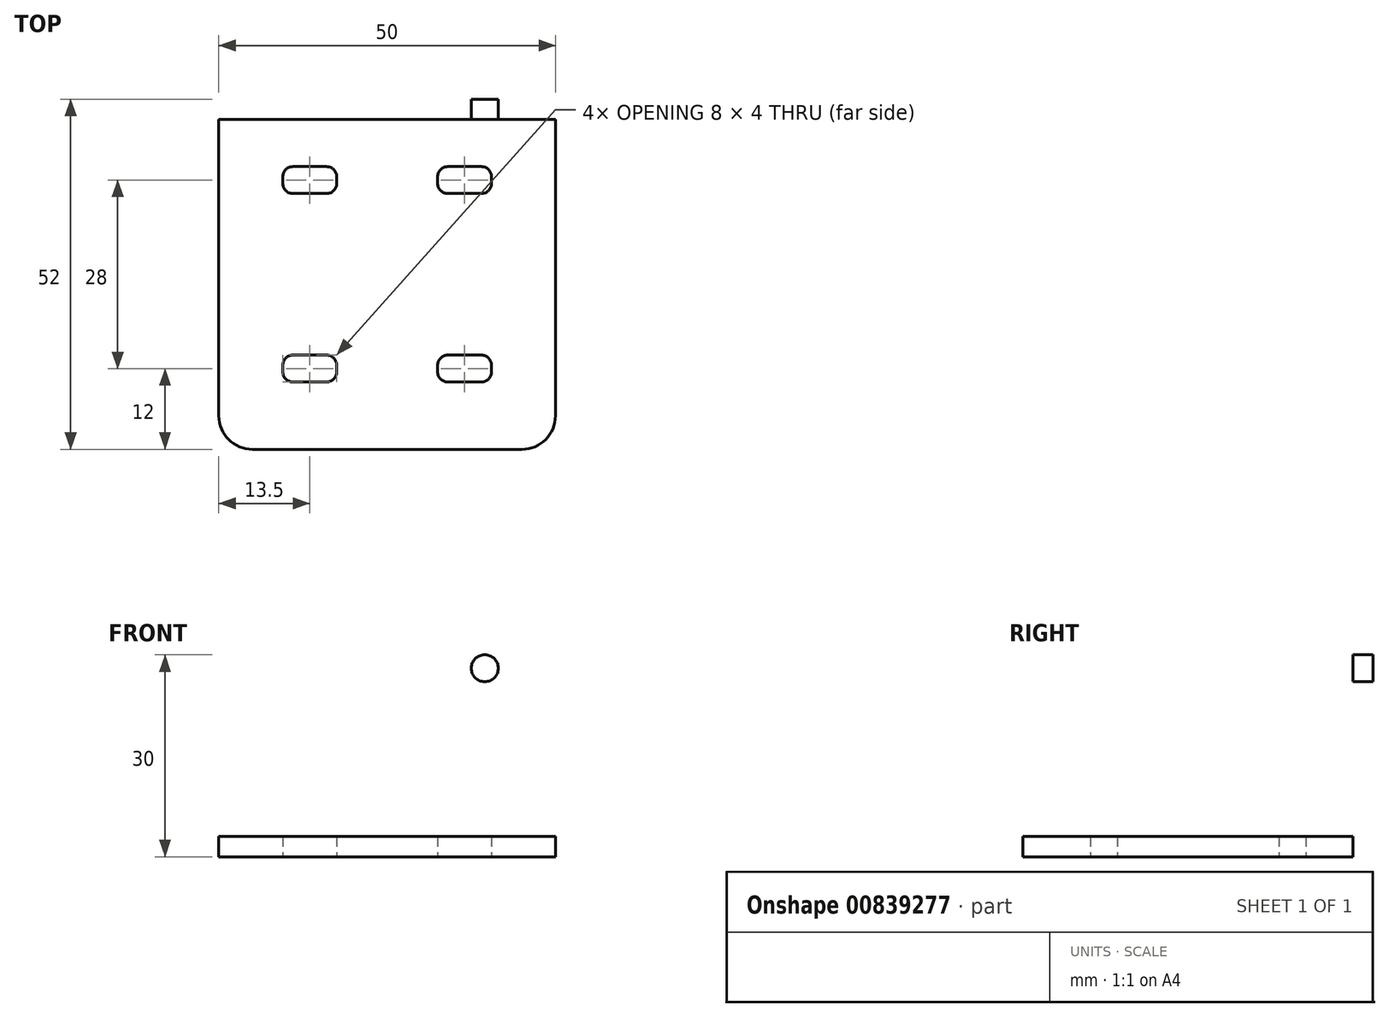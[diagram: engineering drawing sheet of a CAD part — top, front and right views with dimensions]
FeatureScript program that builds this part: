
annotation { "Feature Type Name" : "Feature", "Feature Type Description" : "" }
export const myFeature = defineFeature(function(context is Context, id is Id, definition is map)
    precondition{}
    {
        {
            var Q0;
            Q0=qCreatedBy(makeId("Top.planeOp"),FACE);
            var sketch = newSketch(context, id + "F0", { "sketchPlane" : qUnion([Q0])});
            skLineSegment(sketch, "E0", {"start": v(0, 0) * mm, "end": v(25, 0) * mm});
            skLineSegment(sketch, "E1", {"start": v(25, 0) * mm, "end": v(25, -52) * mm});
            skLineSegment(sketch, "E2", {"start": v(25, -52) * mm, "end": v(-25, -52) * mm});
            skLineSegment(sketch, "E3", {"start": v(-25, -52) * mm, "end": v(-25, 0) * mm});
            skLineSegment(sketch, "E4", {"start": v(-25, 0) * mm, "end": v(0, 0) * mm});
            skLineSegment(sketch, "E5.bottom", {"start": v(-9, -42) * mm, "end": v(-14, -42) * mm});
            skLineSegment(sketch, "E5.top", {"start": v(-9, -38) * mm, "end": v(-14, -38) * mm});
            skLineSegment(sketch, "E5.left", {"start": v(-7.5, -40.5) * mm, "end": v(-7.5, -39.5) * mm});
            skLineSegment(sketch, "E5.right", {"start": v(-15.5, -40.5) * mm, "end": v(-15.5, -39.5) * mm});
            skPoint(sketch, "E5.middle", {"position": v(-11.5, -40) * mm});
            skLineSegment(sketch, "E6.MirrorCS", {"start": v(15.5, -40.5) * mm, "end": v(15.5, -39.5) * mm});
            skPoint(sketch, "E7.MirrorP", {"position": v(11.5, -40) * mm});
            skLineSegment(sketch, "E8.MirrorCS", {"start": v(9, -38) * mm, "end": v(14, -38) * mm});
            skLineSegment(sketch, "E9.MirrorCS", {"start": v(7.5, -40.5) * mm, "end": v(7.5, -39.5) * mm});
            skLineSegment(sketch, "E10.MirrorCS", {"start": v(9, -42) * mm, "end": v(14, -42) * mm});
            skLineSegment(sketch, "E11", {"start": v(25, -26) * mm, "end": v(-25, -26) * mm});
            skLineSegment(sketch, "E12.MirrorCS", {"start": v(-9, -14) * mm, "end": v(-14, -14) * mm});
            skLineSegment(sketch, "E13.MirrorCS", {"start": v(-15.5, -11.5) * mm, "end": v(-15.5, -12.5) * mm});
            skLineSegment(sketch, "E14.MirrorCS", {"start": v(9, -14) * mm, "end": v(14, -14) * mm});
            skLineSegment(sketch, "E15.MirrorCS", {"start": v(9, -10) * mm, "end": v(14, -10) * mm});
            skLineSegment(sketch, "E16.MirrorCS", {"start": v(-9, -10) * mm, "end": v(-14, -10) * mm});
            skLineSegment(sketch, "E17.MirrorCS", {"start": v(-7.5, -11.5) * mm, "end": v(-7.5, -12.5) * mm});
            skPoint(sketch, "E18.MirrorP", {"position": v(-11.5, -12) * mm});
            skLineSegment(sketch, "E19.MirrorCS", {"start": v(7.5, -11.5) * mm, "end": v(7.5, -12.5) * mm});
            skPoint(sketch, "E20.MirrorP", {"position": v(11.5, -12) * mm});
            skLineSegment(sketch, "E21.MirrorCS", {"start": v(15.5, -11.5) * mm, "end": v(15.5, -12.5) * mm});
            skPoint(sketch, "E22.visualSharp", {"position": v(-15.5, -38) * mm});
            skArc(sketch, "E22.filletArc", {"start": v(-14, -38) * mm, "mid": v(-15.06, -38.44) * mm, "end": v(-15.5, -39.5) * mm});
            skPoint(sketch, "E23.visualSharp", {"position": v(-15.5, -42) * mm});
            skArc(sketch, "E23.filletArc", {"start": v(-15.5, -40.5) * mm, "mid": v(-15.06, -41.56) * mm, "end": v(-14, -42) * mm});
            skPoint(sketch, "E24.visualSharp", {"position": v(-7.5, -38) * mm});
            skArc(sketch, "E24.filletArc", {"start": v(-7.5, -39.5) * mm, "mid": v(-7.94, -38.44) * mm, "end": v(-9, -38) * mm});
            skPoint(sketch, "E25.visualSharp", {"position": v(-7.5, -42) * mm});
            skArc(sketch, "E25.filletArc", {"start": v(-9, -42) * mm, "mid": v(-7.94, -41.56) * mm, "end": v(-7.5, -40.5) * mm});
            skPoint(sketch, "E26.visualSharp", {"position": v(7.5, -38) * mm});
            skArc(sketch, "E26.filletArc", {"start": v(9, -38) * mm, "mid": v(7.94, -38.44) * mm, "end": v(7.5, -39.5) * mm});
            skPoint(sketch, "E27.visualSharp", {"position": v(7.5, -42) * mm});
            skArc(sketch, "E27.filletArc", {"start": v(7.5, -40.5) * mm, "mid": v(7.94, -41.56) * mm, "end": v(9, -42) * mm});
            skPoint(sketch, "E28.visualSharp", {"position": v(15.5, -42) * mm});
            skArc(sketch, "E28.filletArc", {"start": v(14, -42) * mm, "mid": v(15.06, -41.56) * mm, "end": v(15.5, -40.5) * mm});
            skPoint(sketch, "E29.visualSharp", {"position": v(15.5, -38) * mm});
            skArc(sketch, "E29.filletArc", {"start": v(15.5, -39.5) * mm, "mid": v(15.06, -38.44) * mm, "end": v(14, -38) * mm});
            skPoint(sketch, "E30.visualSharp", {"position": v(7.5, -10) * mm});
            skArc(sketch, "E30.filletArc", {"start": v(9, -10) * mm, "mid": v(7.94, -10.44) * mm, "end": v(7.5, -11.5) * mm});
            skPoint(sketch, "E31.visualSharp", {"position": v(7.5, -14) * mm});
            skArc(sketch, "E31.filletArc", {"start": v(7.5, -12.5) * mm, "mid": v(7.94, -13.56) * mm, "end": v(9, -14) * mm});
            skPoint(sketch, "E32.visualSharp", {"position": v(15.5, -14) * mm});
            skArc(sketch, "E32.filletArc", {"start": v(14, -14) * mm, "mid": v(15.06, -13.56) * mm, "end": v(15.5, -12.5) * mm});
            skPoint(sketch, "E33.visualSharp", {"position": v(15.5, -10) * mm});
            skArc(sketch, "E33.filletArc", {"start": v(15.5, -11.5) * mm, "mid": v(15.06, -10.44) * mm, "end": v(14, -10) * mm});
            skPoint(sketch, "E34.visualSharp", {"position": v(-7.5, -10) * mm});
            skArc(sketch, "E34.filletArc", {"start": v(-7.5, -11.5) * mm, "mid": v(-7.94, -10.44) * mm, "end": v(-9, -10) * mm});
            skPoint(sketch, "E35.visualSharp", {"position": v(-7.5, -14) * mm});
            skArc(sketch, "E35.filletArc", {"start": v(-9, -14) * mm, "mid": v(-7.94, -13.56) * mm, "end": v(-7.5, -12.5) * mm});
            skPoint(sketch, "E36.visualSharp", {"position": v(-15.5, -14) * mm});
            skArc(sketch, "E36.filletArc", {"start": v(-15.5, -12.5) * mm, "mid": v(-15.06, -13.56) * mm, "end": v(-14, -14) * mm});
            skPoint(sketch, "E37.visualSharp", {"position": v(-15.5, -10) * mm});
            skArc(sketch, "E37.filletArc", {"start": v(-14, -10) * mm, "mid": v(-15.06, -10.44) * mm, "end": v(-15.5, -11.5) * mm});
            skSolve(sketch);
        }
        {
            var Q0;
            {var subQ1=sQuery(id+"F0.wireOp",EDGE,"E0");Q0=makeQuery(id+"F0.imprint","IMPRINT",FACE,{"disambiguationData":[TD([[makeQuery(id+"F0.imprint","IMPRINT",EDGE,{"derivedFrom":subQ1}),-1.0]])]});}
            var Q1;
            {var subQ0=sQuery(id+"F0.wireOp",EDGE,"E2");Q1=makeQuery(id+"F0.imprint","IMPRINT",FACE,{"disambiguationData":[TD([[makeQuery(id+"F0.imprint","IMPRINT",EDGE,{"derivedFrom":subQ0}),-1.0]])]});}
            extrude(context, id + "F1", {"entities" : qUnion([Q0, Q1]), "depth" : 3 * mm, "offsetDistance" : 25 * mm});
        }
        {
            var Q0;
            Q0=makeQuery(id+"F1.opExtrude","CAP_FACE",FACE,{"disambiguationData":[OSD([sQuery(id+"F0.wireOp",EDGE,"E0"),sQuery(id+"F0.wireOp",EDGE,"E1"),sQuery(id+"F0.wireOp",EDGE,"E2"),sQuery(id+"F0.wireOp",EDGE,"E3"),sQuery(id+"F0.wireOp",EDGE,"E4"),sQuery(id+"F0.wireOp",EDGE,"E5.bottom"),sQuery(id+"F0.wireOp",EDGE,"E5.top"),sQuery(id+"F0.wireOp",EDGE,"E5.left"),sQuery(id+"F0.wireOp",EDGE,"E5.right"),sQuery(id+"F0.wireOp",EDGE,"E6.MirrorCS"),sQuery(id+"F0.wireOp",EDGE,"E8.MirrorCS"),sQuery(id+"F0.wireOp",EDGE,"E9.MirrorCS"),sQuery(id+"F0.wireOp",EDGE,"E10.MirrorCS"),sQuery(id+"F0.wireOp",EDGE,"E12.MirrorCS"),sQuery(id+"F0.wireOp",EDGE,"E13.MirrorCS"),sQuery(id+"F0.wireOp",EDGE,"E14.MirrorCS"),sQuery(id+"F0.wireOp",EDGE,"E15.MirrorCS"),sQuery(id+"F0.wireOp",EDGE,"E16.MirrorCS"),sQuery(id+"F0.wireOp",EDGE,"E17.MirrorCS"),sQuery(id+"F0.wireOp",EDGE,"E19.MirrorCS"),sQuery(id+"F0.wireOp",EDGE,"E21.MirrorCS"),sQuery(id+"F0.wireOp",EDGE,"E22.filletArc"),sQuery(id+"F0.wireOp",EDGE,"E23.filletArc"),sQuery(id+"F0.wireOp",EDGE,"E24.filletArc"),sQuery(id+"F0.wireOp",EDGE,"E25.filletArc"),sQuery(id+"F0.wireOp",EDGE,"E26.filletArc"),sQuery(id+"F0.wireOp",EDGE,"E27.filletArc"),sQuery(id+"F0.wireOp",EDGE,"E28.filletArc"),sQuery(id+"F0.wireOp",EDGE,"E29.filletArc"),sQuery(id+"F0.wireOp",EDGE,"E30.filletArc"),sQuery(id+"F0.wireOp",EDGE,"E31.filletArc"),sQuery(id+"F0.wireOp",EDGE,"E32.filletArc"),sQuery(id+"F0.wireOp",EDGE,"E33.filletArc"),sQuery(id+"F0.wireOp",EDGE,"E34.filletArc"),sQuery(id+"F0.wireOp",EDGE,"E35.filletArc"),sQuery(id+"F0.wireOp",EDGE,"E36.filletArc"),sQuery(id+"F0.wireOp",EDGE,"E37.filletArc")])],"isStart":false});
            var sketch = newSketch(context, id + "F2", { "sketchPlane" : qUnion([Q0])});
            skLineSegment(sketch, "E38.bottom", {"start": v(-25, 0) * mm, "end": v(25, 0) * mm});
            skLineSegment(sketch, "E38.top", {"start": v(-25, -3) * mm, "end": v(25, -3) * mm});
            skLineSegment(sketch, "E38.left", {"start": v(-25, 0) * mm, "end": v(-25, -3) * mm});
            skLineSegment(sketch, "E38.right", {"start": v(25, 0) * mm, "end": v(25, -3) * mm});
            skSolve(sketch);
        }
        {
            var Q0;
            Q0=makeQuery(id+"F2.imprint","IMPRINT",FACE,{"disambiguationData":[TD([[makeQuery(id+"F2.imprint","IMPRINT",EDGE,{"derivedFrom":sQuery(id+"F2.wireOp",EDGE,"E38.bottom")}),-1.0]])]});
            extrude(context, id + "F3", {"entities" : qUnion([Q0]), "operationType" : NewBodyOperationType.ADD, "depth" : 49 * mm, "offsetDistance" : 25 * mm});
        }
        {
            var Q0;
            Q0=makeQuery(id+"F3.boolean.opBoolean","MERGE",FACE,{"derivedFrom":[makeQuery(id+"F1.opExtrude","SWEPT_FACE",FACE,{"disambiguationData":[OSD([sQuery(id+"F0.wireOp",EDGE,"E0"),sQuery(id+"F0.wireOp",EDGE,"E4")])]}),makeQuery(id+"F3.opExtrude","SWEPT_FACE",FACE,{"disambiguationData":[OSD([sQuery(id+"F2.wireOp",EDGE,"E38.bottom")])]})]});
            var sketch = newSketch(context, id + "F4", { "sketchPlane" : qUnion([Q0])});
            skCircle(sketch, "E39", {"center": v(0, 28) * mm, "radius": 8.8 * mm});
            skCircle(sketch, "E40", {"center": v(14.5, 28) * mm, "radius": 2 * mm});
            skCircle(sketch, "E41.MirrorC", {"center": v(-14.5, 28) * mm, "radius": 2 * mm});
            skSolve(sketch);
        }
        {
            var Q0;
            Q0=makeQuery(id+"F4.imprint","IMPRINT",FACE,{"disambiguationData":[TD([[makeQuery(id+"F4.imprint","IMPRINT",EDGE,{"derivedFrom":sQuery(id+"F4.wireOp",EDGE,"E41.MirrorC")}),-1.0]])]});
            var Q1;
            Q1=makeQuery(id+"F4.imprint","IMPRINT",FACE,{"disambiguationData":[TD([[makeQuery(id+"F4.imprint","IMPRINT",EDGE,{"derivedFrom":sQuery(id+"F4.wireOp",EDGE,"E39")}),1.0]])]});
            var Q2;
            Q2=makeQuery(id+"F4.imprint","IMPRINT",FACE,{"disambiguationData":[TD([[makeQuery(id+"F4.imprint","IMPRINT",EDGE,{"derivedFrom":sQuery(id+"F4.wireOp",EDGE,"E40")}),1.0]])]});
            extrude(context, id + "F5", {"entities" : qUnion([Q0, Q1, Q2]), "operationType" : NewBodyOperationType.REMOVE, "oppositeDirection" : true, "depth" : 3 * mm, "offsetDistance" : 25 * mm});
        }
        {
            var Q0;
            Q0=makeQuery(id+"F3.opExtrude","CAP_EDGE",EDGE,{"disambiguationData":[OSD([sQuery(id+"F2.wireOp",EDGE,"E38.left")])],"isStart":false});
            var Q1;
            Q1=makeQuery(id+"F3.opExtrude","CAP_EDGE",EDGE,{"disambiguationData":[OSD([sQuery(id+"F2.wireOp",EDGE,"E38.right")])],"isStart":false});
            var Q2;
            Q2=makeQuery(id+"F1.opExtrude","SWEPT_EDGE",EDGE,{"disambiguationData":[OSD([sQuery(id+"F0.wireOp",EDGE,"E2"),sQuery(id+"F0.wireOp",EDGE,"E3")])]});
            var Q3;
            Q3=makeQuery(id+"F1.opExtrude","SWEPT_EDGE",EDGE,{"disambiguationData":[OSD([sQuery(id+"F0.wireOp",EDGE,"E1"),sQuery(id+"F0.wireOp",EDGE,"E2")])]});
            fillet(context, id + "F6", {"entities" : qUnion([Q0, Q1, Q2, Q3]), "radius" : 5 * mm, "tangentPropagation" : true, "allowEdgeOverflow" : false});
        }
    });
